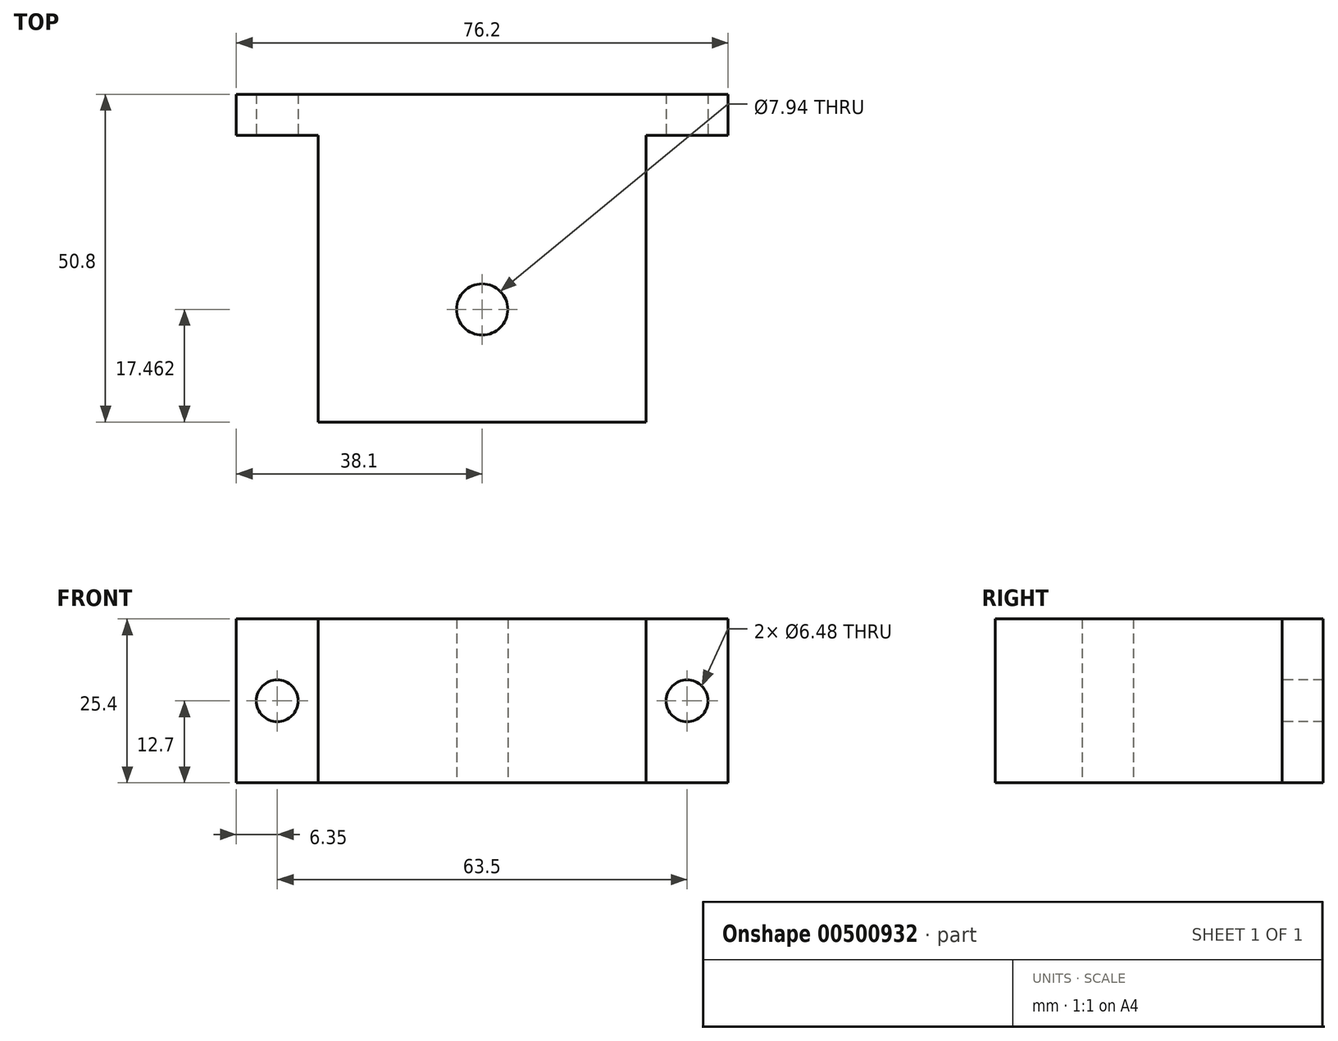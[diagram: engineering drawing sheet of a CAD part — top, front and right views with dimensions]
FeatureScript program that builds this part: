
annotation { "Feature Type Name" : "Feature", "Feature Type Description" : "" }
export const myFeature = defineFeature(function(context is Context, id is Id, definition is map)
    precondition{}
    {
        {
            var Q0;
            Q0=qCreatedBy(makeId("Top.planeOp"),FACE);
            var sketch = newSketch(context, id + "F0", { "sketchPlane" : qUnion([Q0])});
            skLineSegment(sketch, "E0", {"start": v(0, 0) * mm, "end": v(76.2, 0) * mm});
            skLineSegment(sketch, "E1", {"start": v(76.2, 0) * mm, "end": v(76.2, -6.35) * mm});
            skLineSegment(sketch, "E2", {"start": v(76.2, -6.35) * mm, "end": v(63.5, -6.35) * mm});
            skLineSegment(sketch, "E3", {"start": v(63.5, -6.35) * mm, "end": v(63.5, -50.8) * mm});
            skLineSegment(sketch, "E4", {"start": v(63.5, -50.8) * mm, "end": v(12.7, -50.8) * mm});
            skLineSegment(sketch, "E5", {"start": v(12.7, -50.8) * mm, "end": v(12.7, -6.35) * mm});
            skLineSegment(sketch, "E6", {"start": v(12.7, -6.35) * mm, "end": v(0, -6.35) * mm});
            skLineSegment(sketch, "E7", {"start": v(0, -6.35) * mm, "end": v(0, 0) * mm});
            skSolve(sketch);
        }
        {
            var Q0;
            Q0=makeQuery(id+"F0.imprint","IMPRINT",FACE,{"disambiguationData":[TD([[makeQuery(id+"F0.imprint","IMPRINT",EDGE,{"derivedFrom":sQuery(id+"F0.wireOp",EDGE,"E0")}),-1.0]])]});
            extrude(context, id + "F1", {"entities" : qUnion([Q0]), "depth" : 25.4 * mm, "offsetDistance" : 25.4 * mm});
        }
        {
            var Q0;
            Q0=makeQuery(id+"F1.opExtrude","SWEPT_FACE",FACE,{"disambiguationData":[OSD([sQuery(id+"F0.wireOp",EDGE,"E2")])]});
            var sketch = newSketch(context, id + "F2", { "sketchPlane" : qUnion([Q0])});
            skSolve(sketch);
        }
        {
            var Q0;
            {var subQ0=sQuery(id+"F0.wireOp",EDGE,"E2");Q0=makeQuery(id+"F2.imprint","IMPRINT",FACE,{"disambiguationData":[TD([[makeQuery(id+"F2.imprint","IMPRINT",EDGE,{"derivedFrom":makeQuery(id+"F1.opExtrude","CAP_EDGE",EDGE,{"disambiguationData":[OSD([subQ0])],"isStart":true})}),-1.0]])]});}
            var sketch = newSketch(context, id + "F3", { "sketchPlane" : qUnion([Q0])});
            skCircle(sketch, "E8", {"center": v(69.85, 12.7) * mm, "radius": 3.24 * mm});
            skSolve(sketch);
        }
        {
            var Q0;
            Q0=makeQuery(id+"F1.opExtrude","SWEPT_FACE",FACE,{"disambiguationData":[OSD([sQuery(id+"F0.wireOp",EDGE,"E6")])]});
            var sketch = newSketch(context, id + "F4", { "sketchPlane" : qUnion([Q0])});
            skCircle(sketch, "E9", {"center": v(6.35, 12.7) * mm, "radius": 3.24 * mm});
            skPoint(sketch, "E9.centerSnap0", {"position": v(0, 12.7) * mm});
            skSolve(sketch);
        }
        {
            var Q0;
            Q0=makeQuery(id+"F4.imprint","IMPRINT",FACE,{"disambiguationData":[TD([[makeQuery(id+"F4.imprint","IMPRINT",EDGE,{"derivedFrom":sQuery(id+"F4.wireOp",EDGE,"E9")}),1.0]])]});
            extrude(context, id + "F5", {"entities" : qUnion([Q0]), "operationType" : NewBodyOperationType.REMOVE, "oppositeDirection" : true, "depth" : 25.4 * mm, "offsetDistance" : 25.4 * mm});
        }
        {
            var Q0;
            Q0=makeQuery(id+"F3.imprint","IMPRINT",FACE,{"disambiguationData":[TD([[makeQuery(id+"F3.imprint","IMPRINT",EDGE,{"derivedFrom":sQuery(id+"F3.wireOp",EDGE,"E8")}),1.0]])]});
            extrude(context, id + "F6", {"entities" : qUnion([Q0]), "operationType" : NewBodyOperationType.REMOVE, "oppositeDirection" : true, "depth" : 25.4 * mm, "offsetDistance" : 25.4 * mm});
        }
        {
            var Q0;
            Q0=makeQuery(id+"F1.opExtrude","CAP_FACE",FACE,{"disambiguationData":[OSD([sQuery(id+"F0.wireOp",EDGE,"E0"),sQuery(id+"F0.wireOp",EDGE,"E1"),sQuery(id+"F0.wireOp",EDGE,"E2"),sQuery(id+"F0.wireOp",EDGE,"E3"),sQuery(id+"F0.wireOp",EDGE,"E4"),sQuery(id+"F0.wireOp",EDGE,"E5"),sQuery(id+"F0.wireOp",EDGE,"E6"),sQuery(id+"F0.wireOp",EDGE,"E7")])],"isStart":false});
            var sketch = newSketch(context, id + "F7", { "sketchPlane" : qUnion([Q0])});
            skCircle(sketch, "E10", {"center": v(38.1, -33.34) * mm, "radius": 3.81 * mm});
            skSolve(sketch);
        }
        {
            var Q0;
            Q0=sQuery(id+"F7.wireOp",VERTEX,"E10.center");
            var Q1;
            Q1=makeQuery(id+"F1.opExtrude","SWEPT_BODY",BODY,{"disambiguationData":[OSD([sQuery(id+"F0.wireOp",EDGE,"E0"),sQuery(id+"F0.wireOp",EDGE,"E1"),sQuery(id+"F0.wireOp",EDGE,"E2"),sQuery(id+"F0.wireOp",EDGE,"E3"),sQuery(id+"F0.wireOp",EDGE,"E4"),sQuery(id+"F0.wireOp",EDGE,"E5"),sQuery(id+"F0.wireOp",EDGE,"E6"),sQuery(id+"F0.wireOp",EDGE,"E7")])]});
            hole(context, id + "F8", {"style" : HoleStyle.SIMPLE, "endStyle" : HoleEndStyle.THROUGH, "standardTappedOrClearance" : lookupTablePath({ "standard" : "ANSI", "engagement" : "75%", "pitch" : "16 tpi", "size" : "3/8", "type" : "Tapped" }), "standardBlindInLast" : lookupTablePath({ "standard" : "ANSI", "engagement" : "75%", "pitch" : "16 tpi", "size" : "3/8", "type" : "Tapped" }), "holeDiameter" : 7.94 * mm, "showTappedDepth" : true, "isTappedThrough" : true, "tappedDepth" : 12.7 * mm, "tapClearance" : 3, "locations" : qUnion([Q0]), "scope" : qUnion([Q1]), "majorDiameter" : 9.53 * mm, "startStyle" : HoleStartStyle.PART});
        }
    });
